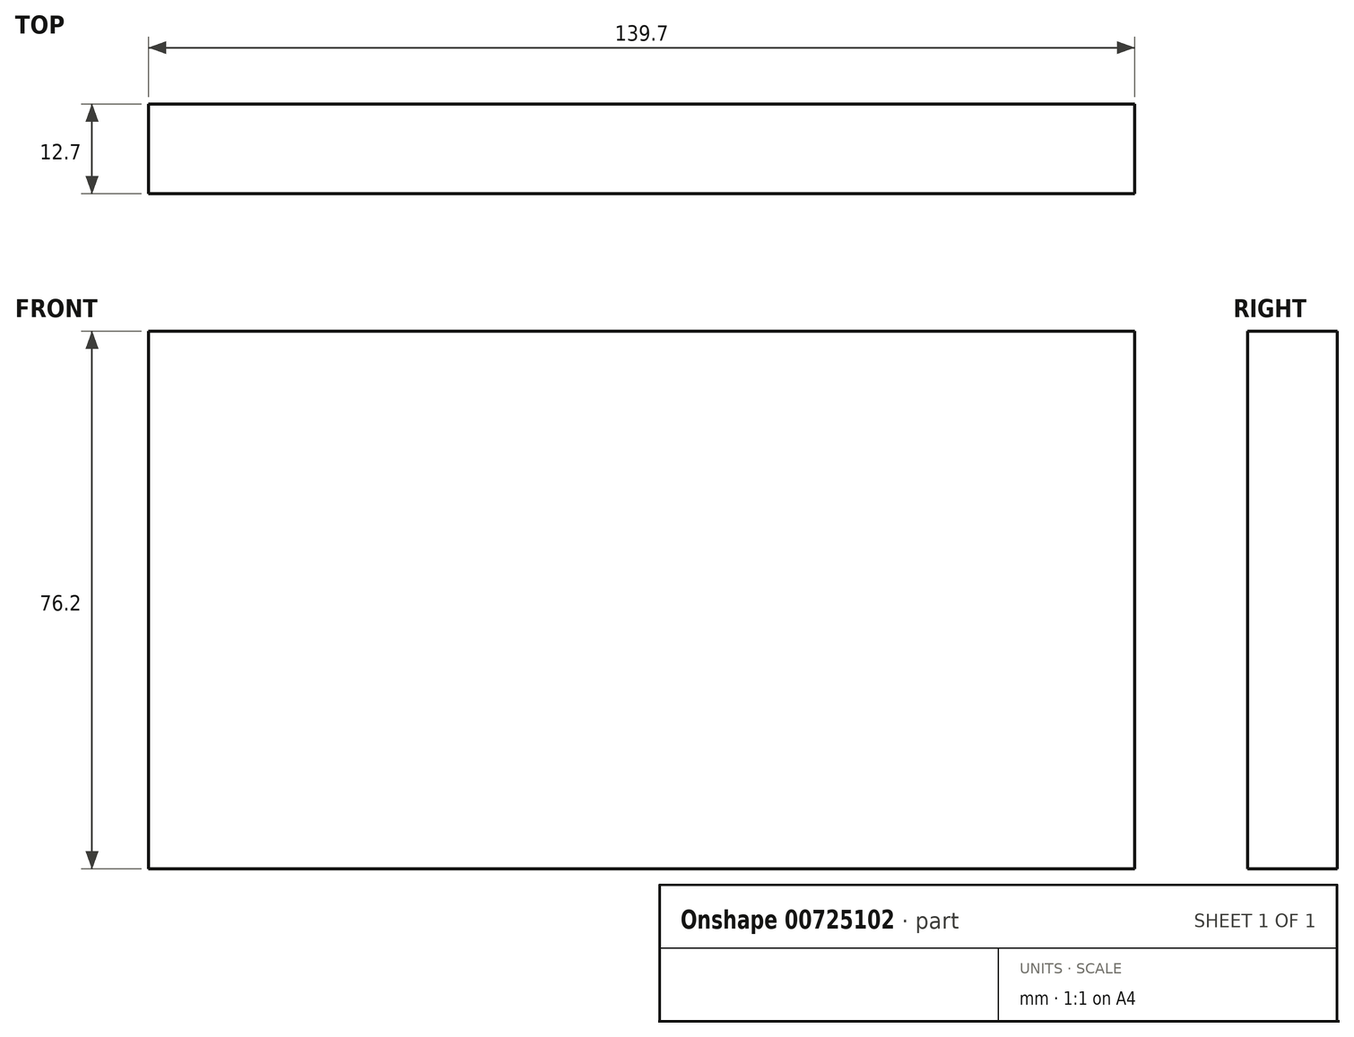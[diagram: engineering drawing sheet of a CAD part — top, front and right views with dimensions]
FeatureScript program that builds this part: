
annotation { "Feature Type Name" : "Feature", "Feature Type Description" : "" }
export const myFeature = defineFeature(function(context is Context, id is Id, definition is map)
    precondition{}
    {
        {
            var Q0;
            Q0=qCreatedBy(makeId("Front.planeOp"),FACE);
            var sketch = newSketch(context, id + "F0", { "sketchPlane" : qUnion([Q0])});
            skLineSegment(sketch, "E0.bottom", {"start": v(-61.9, 76.2) * mm, "end": v(77.8, 76.2) * mm});
            skLineSegment(sketch, "E0.top", {"start": v(-61.9, 0) * mm, "end": v(77.8, 0) * mm});
            skLineSegment(sketch, "E0.left", {"start": v(-61.9, 76.2) * mm, "end": v(-61.9, 0) * mm});
            skLineSegment(sketch, "E0.right", {"start": v(77.8, 76.2) * mm, "end": v(77.8, 0) * mm});
            skSolve(sketch);
        }
        {
            var Q0;
            Q0=makeQuery(id+"F0.imprint","IMPRINT",FACE,{"disambiguationData":[TD([[makeQuery(id+"F0.imprint","IMPRINT",EDGE,{"derivedFrom":sQuery(id+"F0.wireOp",EDGE,"E0.bottom")}),-1.0]])]});
            extrude(context, id + "F1", {"entities" : qUnion([Q0]), "depth" : 12.7 * mm, "offsetDistance" : 25.4 * mm});
        }
    });
